# Revit family: Haworth_Intuity_BaseFeedCover
name_source: partatom
category: Furniture Systems
revit_build: Autodesk Revit 2018 (Build: 20170223_1515(x64)
units: mm (PartAtom-declared; Revit-internal decimal feet)

## family parameters
Always vertical = Yes
Cut with Voids When Loaded = No
OmniClass Number = 23.40.70.14.64.21
OmniClass Title = Systems Furniture
Part Type = Normal
Room Calculation Point = No
Round Connector Dimension = Use Diameter
Shared = No
Work Plane-Based = No

## types (1)
- Base Feed Cover
    Actual Depth = 2"
    Actual Height = 28"
    Actual Width = 4 1/4"
    Assembly Code = E2020200
    Bracket Finish = Haworth _ Paint _ Graphite
    Description = Haworth - Intuity - Base Feed Cover
    Manufacturer = Haworth
    Model = Intuity
    Revision Number = 1
    Size = Verify Final Dim. w/ Haworth
    Support Finish = Haworth _ Paint _ Metallic Silver
    Support Inset = 1/4"
    URL = www.haworth.com
    URL - Product = https://www.haworth.com
    Warranty = https://library.haworth.com

## geometry (parser evidence)
native form markers: Sweep x2
no freeform markers — native parametric forms only
